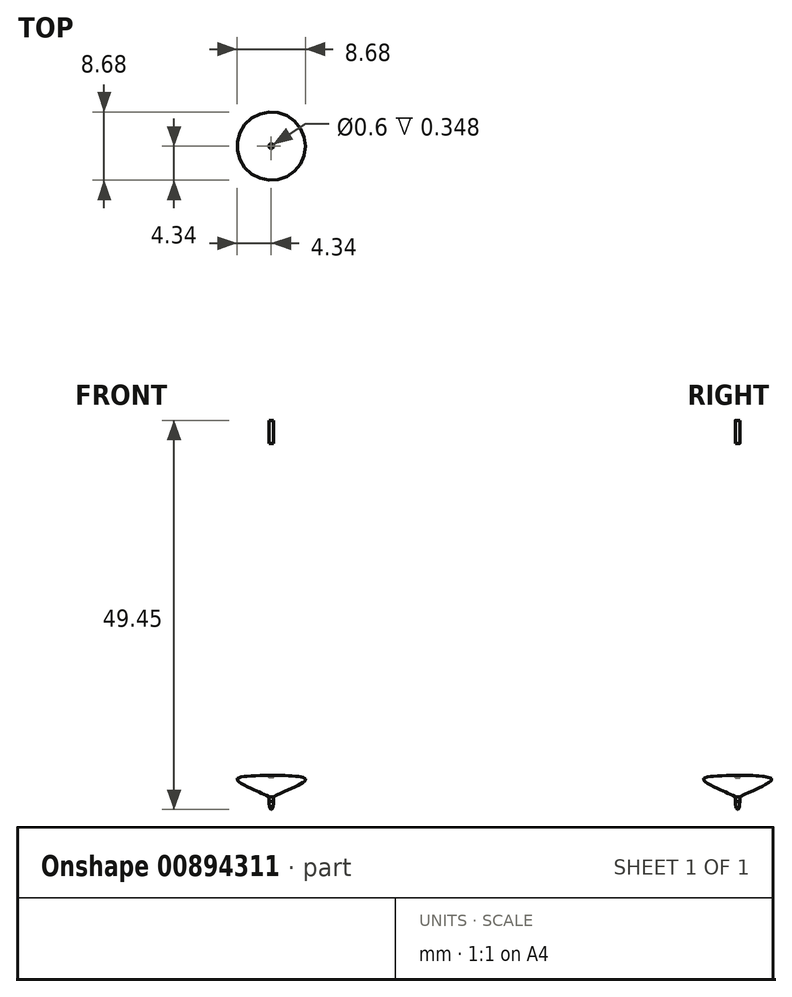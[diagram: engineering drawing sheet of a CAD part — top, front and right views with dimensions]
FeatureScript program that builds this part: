
annotation { "Feature Type Name" : "Feature", "Feature Type Description" : "" }
export const myFeature = defineFeature(function(context is Context, id is Id, definition is map)
    precondition{}
    {
        {
            var Q0;
            Q0=qCreatedBy(makeId("Right.planeOp"),FACE);
            var sketch = newSketch(context, id + "F0", { "sketchPlane" : qUnion([Q0])});
            skLineSegment(sketch, "E0", {"start": v(0, -42.5) * mm, "end": v(0, -46.53) * mm});
            skFitSpline(sketch, "E1", {"points": [v(-0.3, -42.16) * mm, v(-4.34, -42.67) * mm, v(-0.3, -44.9) * mm], "startDerivative": vector(-10.18, -0.3) * mm, "endDerivative": vector(9.9, -5.12) * mm});
            skLineSegment(sketch, "E2", {"start": v(-0.3, -44.9) * mm, "end": v(-0.3, -45.46) * mm});
            skFitSpline(sketch, "E3", {"points": [v(-0.3, -45.46) * mm, v(0, -46.53) * mm], "startDerivative": vector(0.3, -1.07) * mm, "endDerivative": vector(1.08, -0.75) * mm});
            skLineSegment(sketch, "E4", {"start": v(-0.3, -42.16) * mm, "end": v(-0.3, -42.5) * mm});
            skLineSegment(sketch, "E5", {"start": v(-0.3, -42.5) * mm, "end": v(0, -42.5) * mm});
            skLineSegment(sketch, "E6", {"start": v(-2.88, -48.1) * mm, "end": v(-2.88, -48.46) * mm});
            skLineSegment(sketch, "E7", {"start": v(-2.88, -48.1) * mm, "end": v(-4.99, -48.1) * mm});
            skLineSegment(sketch, "E8", {"start": v(-4.99, -48.1) * mm, "end": v(-4.99, -48.46) * mm});
            skLineSegment(sketch, "E9", {"start": v(-4.99, -48.46) * mm, "end": v(-2.88, -48.46) * mm});
            skSolve(sketch);
        }
        {
            var Q0;
            Q0=makeQuery(id+"F0.imprint","IMPRINT",FACE,{"disambiguationData":[TD([[makeQuery(id+"F0.imprint","IMPRINT",EDGE,{"derivedFrom":sQuery(id+"F0.wireOp",EDGE,"E0")}),-1.0]])]});
            var Q1;
            Q1=sQuery(id+"F0.wireOp",EDGE,"E0");
            revolve(context, id + "F1", {"surfaceOperationType" : NewSurfaceOperationType.NEW, "entities" : qUnion([Q0]), "axis" : qUnion([Q1]), "revolveType" : RevolveType.FULL});
        }
        {
            var Q0;
            Q0=makeQuery(id+"F0.imprint","IMPRINT",FACE,{"disambiguationData":[TD([[makeQuery(id+"F0.imprint","IMPRINT",EDGE,{"derivedFrom":sQuery(id+"F0.wireOp",EDGE,"E6")}),-1.0]])]});
            var Q1;
            Q1=sQuery(id+"F0.wireOp",EDGE,"E9");
            revolve(context, id + "F2", {"surfaceOperationType" : NewSurfaceOperationType.NEW, "entities" : qUnion([Q0]), "axis" : qUnion([Q1]), "revolveType" : RevolveType.FULL});
        }
        {
            var Q0;
            Q0=makeQuery(id+"F2.opRevolve","SWEPT_BODY",BODY,{"disambiguationData":[OSD([sQuery(id+"F0.wireOp",EDGE,"E6"),sQuery(id+"F0.wireOp",EDGE,"E7"),sQuery(id+"F0.wireOp",EDGE,"E8"),sQuery(id+"F0.wireOp",EDGE,"E9")])]});
            deleteBodies(context, id + "F3", {"entities" : qUnion([Q0])});
        }
        {
            var Q0;
            Q0=qCreatedBy(makeId("Top.planeOp"),FACE);
            var sketch = newSketch(context, id + "F4", { "sketchPlane" : qUnion([Q0])});
            skCircle(sketch, "E10", {"center": v(0, 0) * mm, "radius": 0.3 * mm});
            skSolve(sketch);
        }
        {
            var Q0;
            Q0 = qSketchRegion(id + "F4", true);
            extrude(context, id + "F5", {"entities" : qUnion([Q0]), "depth" : 2.92 * mm, "offsetDistance" : 25.4 * mm});
        }
    });
